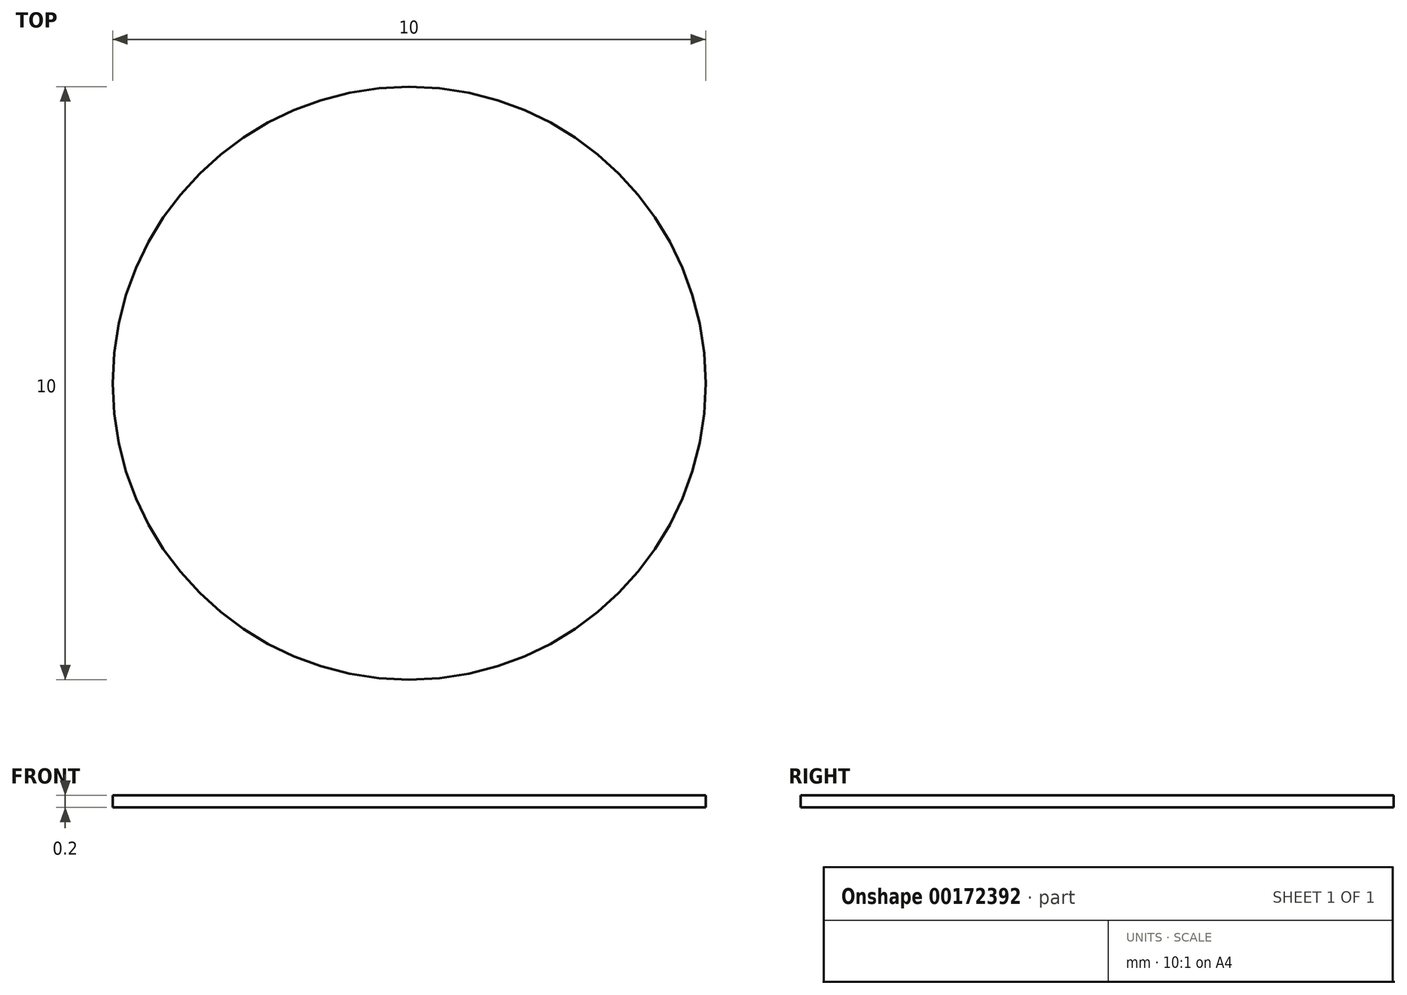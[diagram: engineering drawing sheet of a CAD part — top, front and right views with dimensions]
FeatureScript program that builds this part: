
annotation { "Feature Type Name" : "Feature", "Feature Type Description" : "" }
export const myFeature = defineFeature(function(context is Context, id is Id, definition is map)
    precondition{}
    {
        {
            var Q0;
            Q0=qCreatedBy(makeId("Top.planeOp"),FACE);
            var sketch = newSketch(context, id + "F0", { "sketchPlane" : qUnion([Q0])});
            skCircle(sketch, "E0", {"center": v(0, 0) * mm, "radius": 5 * mm});
            skSolve(sketch);
        }
        {
            var Q0;
            Q0=makeQuery(id+"F0.imprint","IMPRINT",FACE,{"disambiguationData":[TD([[makeQuery(id+"F0.imprint","IMPRINT",EDGE,{"derivedFrom":sQuery(id+"F0.wireOp",EDGE,"E0")}),1.0]])]});
            extrude(context, id + "F1", {"entities" : qUnion([Q0]), "depth" : 0.2 * mm});
        }
    });
